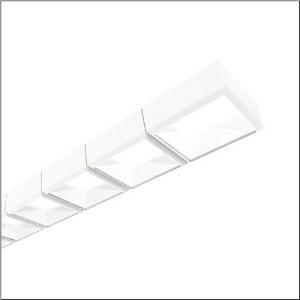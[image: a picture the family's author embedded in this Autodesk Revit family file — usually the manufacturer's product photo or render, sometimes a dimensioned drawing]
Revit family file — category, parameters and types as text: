
# Revit family: scriptus_r__11_5mz223d04wa_758a
name_source: partatom
category: Lighting Fixtures
units: mm (PartAtom-declared; Revit-internal decimal feet)

## family parameters
Cut with Voids When Loaded = No
Host = Face
Light Source = No
Part Type = Normal
Room Calculation Point = No
Round Connector Dimension = Use Diameter
Shared = No

## types (1)
- --- (1 x LED 4000K / CRI = 80 (unbekannt), 7230 lm, 4000K)
    Apparent Load = 51 VA
    CIE Flux Codes = 82 95 99 100 100
    Color Rendering = 80
    Color Temperature = 4000K
    Default Elevation = 1800 mm
    Description = Scriptus® 11, office luminaire, primary optical cover: lenses, CAT 2 (L<= 3000cd/m²), light emission: direct distribution, primary light characteristic: symmetric, installation type: surface-mounted, LED, rated luminous flux: 7.230lm, luminous efficacy: 143lm/W, light colour: 840, colour temperature: 4000K, control gear: DALI, with terminal, 5-pole, mains connection: 230V, AC, 50Hz, rated input power: 51W, housing, luminaire housing, of aluminium, traffic white (RAL 9016), length: 2.426mm, width: 114mm, height: 57mm, protection rating (complete): IP20, insulation class (complete): insulation class I (protective earthing), certification: CE, ENEC, VDE, protection symbol: F, permissible operating ambient temperature: 0..+35°C, standard: EN 50419, packaging unit: 1 piece
    Height = 57 mm
    Lamp = 1 x LED 4000K / CRI >= 80 (unbekannt)
    Lamp Light Flux = 7230 lm
    Lamp count = 1
    Length = 2426 mm
    Luminous efficacy = 143 lm/W
    Manufacturer = Siteco
    ModVariant = No
    Model = 5MZ223D04WA
    Mounting Place = Ceiling
    Mounting Type = Surface mounted
    Number of Poles = 1
    OnlyDefault = Yes
    Power Factor = 1
    Product Name = Scriptus® 11
    Product group = office luminaire | ceiling mounted
    ProductGroupID = 302
    Protection Class = Protection class I
    Protection Degree = IP 20
    RLX_Detail_Level = 1
    RLX_Emergency_Light_Flux = 0 lm
    RLX_Emergency_Type = 0
    RLX_Emergency_Type_DB = No
    RlxData = <blob elided: 31317 chars, md5=7ad4b27c>
    Socket = socket
    Standby Power = 0 W
    System Light Flux = 7230 lm
    System Power = 51 W
    Type Comments = factory setting: luminous flux: 100 % | dim-lin: 254 | 525 mA
    Type Image = l_1004833.jpg
    URL = http://relux.com
    VarID = @adj_203200
    Voltage = 0 V
    Weight = 0.00 kg
    Width = 114 mm

## geometry (parser evidence)
native form markers: Blend x4, Sweep x10
no freeform markers — native parametric forms only
